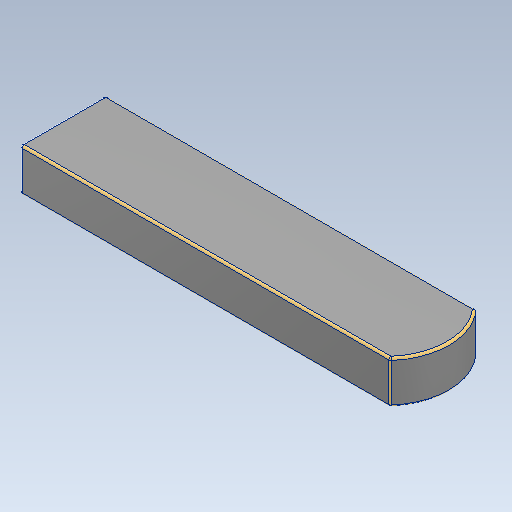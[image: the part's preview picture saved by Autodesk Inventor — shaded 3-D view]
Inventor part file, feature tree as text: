
AUTODESK INVENTOR PART (.ipt)
format: ipt  version: 2021 (Build 250183000, 183)  size: 814,080 bytes
history: mixed  units: mm
features: other x1, fillet x1, imported_body x1
ambient origin geometry x8: Origin, YZ Plane, XZ Plane, XY Plane, X Axis, Y Axis, Z Axis, Center Point
bodies: Body1 (imported_parasolid)
feature tree (3):
  other  "Sólido1"
  fillet  "Redondeo1"  [1 undecoded]
  imported_body  NMx_Import_Brep_tag  [imported B-rep: ~5 faces, bbox_mm=None]
note: 1 required parameter value undecoded (feature->parameter linkage not recoverable at this tier; creation-order binding heuristic only, values carry confidence <= 0.55)
